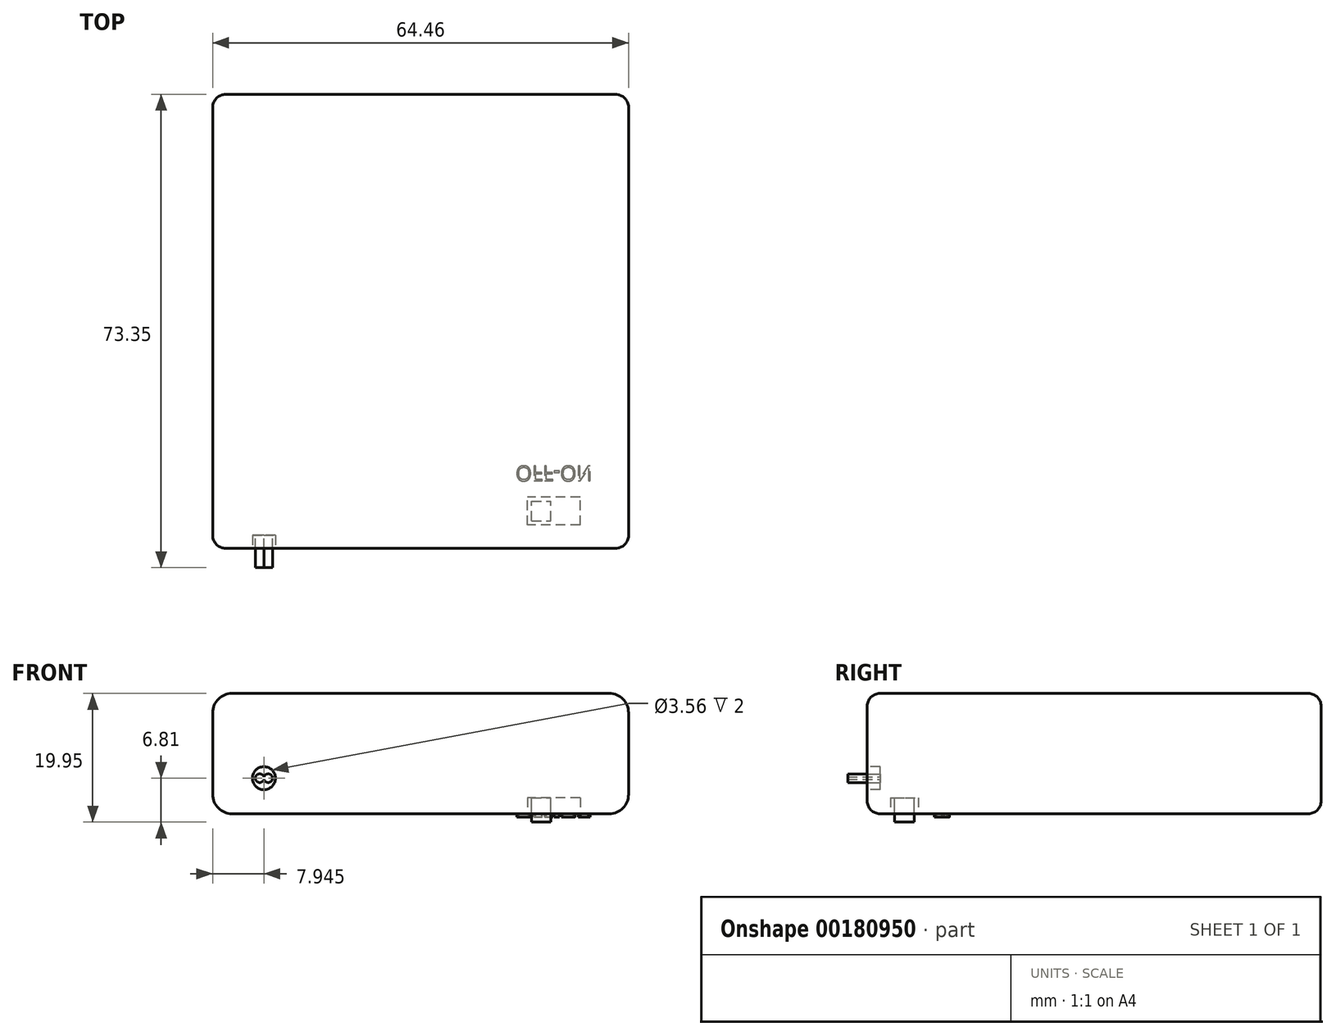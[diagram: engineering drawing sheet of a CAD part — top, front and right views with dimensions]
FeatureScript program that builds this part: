
annotation { "Feature Type Name" : "Feature", "Feature Type Description" : "" }
export const myFeature = defineFeature(function(context is Context, id is Id, definition is map)
    precondition{}
    {
        {
            var Q0;
            Q0=qCreatedBy(makeId("Top.planeOp"),FACE);
            var sketch = newSketch(context, id + "F0", { "sketchPlane" : qUnion([Q0])});
            skLineSegment(sketch, "E0.bottom", {"start": v(32.23, 35.17) * mm, "end": v(-32.23, 35.17) * mm});
            skLineSegment(sketch, "E0.top", {"start": v(32.23, -35.17) * mm, "end": v(-32.23, -35.17) * mm});
            skLineSegment(sketch, "E0.left", {"start": v(32.23, 35.17) * mm, "end": v(32.23, -35.17) * mm});
            skLineSegment(sketch, "E0.right", {"start": v(-32.23, 35.17) * mm, "end": v(-32.23, -35.17) * mm});
            skPoint(sketch, "E0.middle", {"position": v(0, 0) * mm});
            skSolve(sketch);
        }
        {
            var Q0;
            Q0=qSketchRegion(id+"F0",true);
            extrude(context, id + "F1", {"entities" : qUnion([Q0]), "depth" : 18.65 * mm});
        }
        {
            var Q0;
            Q0=makeQuery(id+"F1.opExtrude","CAP_EDGE",EDGE,{"disambiguationData":[OSD([sQuery(id+"F0.wireOp",EDGE,"E0.right")])],"isStart":false});
            var Q1;
            Q1=makeQuery(id+"F1.opExtrude","CAP_EDGE",EDGE,{"disambiguationData":[OSD([sQuery(id+"F0.wireOp",EDGE,"E0.left")])],"isStart":false});
            var Q2;
            Q2=makeQuery(id+"F1.opExtrude","CAP_EDGE",EDGE,{"disambiguationData":[OSD([sQuery(id+"F0.wireOp",EDGE,"E0.left")])],"isStart":true});
            var Q3;
            Q3=makeQuery(id+"F1.opExtrude","CAP_EDGE",EDGE,{"disambiguationData":[OSD([sQuery(id+"F0.wireOp",EDGE,"E0.right")])],"isStart":true});
            fillet(context, id + "F2", {"entities" : qUnion([Q0, Q1, Q2, Q3]), "radius" : 3 * mm, "tangentPropagation" : true, "allowEdgeOverflow" : false});
        }
        {
            var Q0;
            Q0=makeQuery(id+"F1.opExtrude","SWEPT_FACE",FACE,{"disambiguationData":[OSD([sQuery(id+"F0.wireOp",EDGE,"E0.top")])]});
            var Q1;
            Q1=makeQuery(id+"F1.opExtrude","SWEPT_FACE",FACE,{"disambiguationData":[OSD([sQuery(id+"F0.wireOp",EDGE,"E0.bottom")])]});
            fillet(context, id + "F3", {"entities" : qUnion([Q0, Q1]), "radius" : 2 * mm, "tangentPropagation" : true, "allowEdgeOverflow" : false});
        }
        {
            var Q0;
            Q0=makeQuery(id+"F1.opExtrude","CAP_FACE",FACE,{"disambiguationData":[OSD([sQuery(id+"F0.wireOp",EDGE,"E0.bottom"),sQuery(id+"F0.wireOp",EDGE,"E0.top"),sQuery(id+"F0.wireOp",EDGE,"E0.left"),sQuery(id+"F0.wireOp",EDGE,"E0.right")])],"isStart":false});
            var sketch = newSketch(context, id + "F4", { "sketchPlane" : qUnion([Q0])});
            skLineSegment(sketch, "E1.bottom", {"start": v(24.73, 31.57) * mm, "end": v(16.53, 31.57) * mm});
            skLineSegment(sketch, "E1.top", {"start": v(24.73, 27.22) * mm, "end": v(16.53, 27.22) * mm});
            skLineSegment(sketch, "E1.left", {"start": v(24.73, 31.57) * mm, "end": v(24.73, 27.22) * mm});
            skLineSegment(sketch, "E1.right", {"start": v(16.53, 31.57) * mm, "end": v(16.53, 27.22) * mm});
            skSolve(sketch);
        }
        {
            var Q0;
            Q0=qSketchRegion(id+"F4",true);
            extrude(context, id + "F5", {"entities" : qUnion([Q0]), "operationType" : NewBodyOperationType.REMOVE, "oppositeDirection" : true, "depth" : 2.5 * mm});
        }
        {
            var Q0;
            Q0=makeQuery(id+"F5.boolean.opBoolean","COPY",FACE,{"derivedFrom":makeQuery(id+"F5.opExtrude","CAP_FACE",FACE,{"disambiguationData":[OSD([sQuery(id+"F4.wireOp",EDGE,"E1.bottom"),sQuery(id+"F4.wireOp",EDGE,"E1.top"),sQuery(id+"F4.wireOp",EDGE,"E1.left"),sQuery(id+"F4.wireOp",EDGE,"E1.right")])],"isStart":false})});
            var sketch = newSketch(context, id + "F6", { "sketchPlane" : qUnion([Q0])});
            skLineSegment(sketch, "E2", {"start": v(16.53, 29.4) * mm, "end": v(24.73, 29.4) * mm, "construction": true});
            skLineSegment(sketch, "E3.bottom", {"start": v(17.2, 30.9) * mm, "end": v(20.2, 30.9) * mm});
            skLineSegment(sketch, "E3.top", {"start": v(17.2, 27.9) * mm, "end": v(20.2, 27.9) * mm});
            skLineSegment(sketch, "E3.left", {"start": v(17.2, 30.9) * mm, "end": v(17.2, 27.9) * mm});
            skLineSegment(sketch, "E3.right", {"start": v(20.2, 30.9) * mm, "end": v(20.2, 27.9) * mm});
            skPoint(sketch, "E3.middle", {"position": v(18.7, 29.4) * mm});
            skSolve(sketch);
        }
        {
            var Q0;
            Q0=qSketchRegion(id+"F6",true);
            extrude(context, id + "F7", {"entities" : qUnion([Q0]), "operationType" : NewBodyOperationType.ADD, "depth" : (1.3 + 2.5) * mm});
        }
        {
            var Q0;
            Q0=makeQuery(id+"F1.opExtrude","SWEPT_FACE",FACE,{"disambiguationData":[OSD([sQuery(id+"F0.wireOp",EDGE,"E0.bottom")])]});
            var sketch = newSketch(context, id + "F8", { "sketchPlane" : qUnion([Q0])});
            skCircle(sketch, "E4", {"center": v(24.29, 13.14) * mm, "radius": 1.78 * mm});
            skSolve(sketch);
        }
        {
            var Q0;
            Q0=qSketchRegion(id+"F8",true);
            extrude(context, id + "F9", {"entities" : qUnion([Q0]), "operationType" : NewBodyOperationType.REMOVE, "oppositeDirection" : true, "depth" : 2 * mm});
        }
        {
            var Q0;
            Q0=makeQuery(id+"F1.opExtrude","CAP_FACE",FACE,{"disambiguationData":[OSD([sQuery(id+"F0.wireOp",EDGE,"E0.bottom"),sQuery(id+"F0.wireOp",EDGE,"E0.top"),sQuery(id+"F0.wireOp",EDGE,"E0.left"),sQuery(id+"F0.wireOp",EDGE,"E0.right")])],"isStart":false});
            var sketch = newSketch(context, id + "F10", { "sketchPlane" : qUnion([Q0])});
            skText(sketch, "E5", { "text": "OFF-ON", "fontName": "OpenSans-Regular.ttf"});
            skPoint(sketch, "E6", {"position": v(20.63, 27.22) * mm});
            const initialGuessF10  = {"E5": [0.01472, 0.02242, 1, 0, 0.00233]};
            skSetInitialGuess(sketch, initialGuessF10);
            skSolve(sketch);
        }
        {
            var Q0;
            Q0=qSketchRegion(id+"F10",true);
            extrude(context, id + "F11", {"entities" : qUnion([Q0]), "operationType" : NewBodyOperationType.ADD, "depth" : 0.5 * mm});
        }
        {
            var Q0;
            Q0=makeQuery(id+"F1.opExtrude","CAP_FACE",FACE,{"disambiguationData":[OSD([sQuery(id+"F0.wireOp",EDGE,"E0.bottom"),sQuery(id+"F0.wireOp",EDGE,"E0.top"),sQuery(id+"F0.wireOp",EDGE,"E0.left"),sQuery(id+"F0.wireOp",EDGE,"E0.right")])],"isStart":true});
            var sketch = newSketch(context, id + "F12", { "sketchPlane" : qUnion([Q0])});
            skCircle(sketch, "E7", {"center": v(0, 29.19) * mm, "radius": 2.33 * mm});
            skSolve(sketch);
        }
        {
            var Q0;
            Q0=qCreatedBy(makeId("Top.planeOp"),FACE);
            var sketch = newSketch(context, id + "F13", { "sketchPlane" : qUnion([Q0])});
            skLineSegment(sketch, "E8", {"start": v(0, 61.28) * mm, "end": v(0, -59.76) * mm, "construction": true});
            skSolve(sketch);
        }
        {
            var Q0;
            Q0=makeQuery(id+"F1.opExtrude","SWEPT_BODY",BODY,{"disambiguationData":[OSD([sQuery(id+"F0.wireOp",EDGE,"E0.bottom"),sQuery(id+"F0.wireOp",EDGE,"E0.top"),sQuery(id+"F0.wireOp",EDGE,"E0.left"),sQuery(id+"F0.wireOp",EDGE,"E0.right")])]});
            var Q1;
            Q1=sQuery(id+"F13.wireOp",EDGE,"E8");
            transform(context, id + "F14", {"entities" : qUnion([Q0]), "transformType" : TransformType.ROTATION, "transformAxis" : qUnion([Q1]), "angle" : 180 * degree, "makeCopy" : false});
        }
        {
            var Q0;
            Q0=qCreatedBy(makeId("Right.planeOp"),FACE);
            var sketch = newSketch(context, id + "F15", { "sketchPlane" : qUnion([Q0])});
            skLineSegment(sketch, "E9", {"start": v(0, 0) * mm, "end": v(0, 39) * mm, "construction": true});
            skSolve(sketch);
        }
        {
            var Q0;
            Q0=makeQuery(id+"F1.opExtrude","SWEPT_BODY",BODY,{"disambiguationData":[OSD([sQuery(id+"F0.wireOp",EDGE,"E0.bottom"),sQuery(id+"F0.wireOp",EDGE,"E0.top"),sQuery(id+"F0.wireOp",EDGE,"E0.left"),sQuery(id+"F0.wireOp",EDGE,"E0.right")])]});
            var Q1;
            Q1=sQuery(id+"F15.wireOp",EDGE,"E9");
            transform(context, id + "F16", {"entities" : qUnion([Q0]), "transformType" : TransformType.ROTATION, "transformAxis" : qUnion([Q1]), "angle" : 90 * degree, "makeCopy" : false});
        }
        {
            var Q0;
            Q0=qCreatedBy(makeId("Front.planeOp"),FACE);
            var sketch = newSketch(context, id + "F17", { "sketchPlane" : qUnion([Q0])});
            skLineSegment(sketch, "E10", {"start": v(0, 0) * mm, "end": v(0, 59.82) * mm, "construction": true});
            skSolve(sketch);
        }
        {
            var Q0;
            Q0=makeQuery(id+"F1.opExtrude","SWEPT_BODY",BODY,{"disambiguationData":[OSD([sQuery(id+"F0.wireOp",EDGE,"E0.bottom"),sQuery(id+"F0.wireOp",EDGE,"E0.top"),sQuery(id+"F0.wireOp",EDGE,"E0.left"),sQuery(id+"F0.wireOp",EDGE,"E0.right")])]});
            var Q1;
            Q1=sQuery(id+"F17.wireOp",EDGE,"E10");
            transform(context, id + "F18", {"entities" : qUnion([Q0]), "transformType" : TransformType.ROTATION, "transformAxis" : qUnion([Q1]), "angle" : 90 * degree, "makeCopy" : false});
        }
        {
            var Q0;
            Q0=makeQuery(id+"F9.boolean.opBoolean","COPY",FACE,{"derivedFrom":makeQuery(id+"F9.opExtrude","CAP_FACE",FACE,{"disambiguationData":[OSD([sQuery(id+"F8.wireOp",EDGE,"E4")])],"isStart":false})});
            var sketch = newSketch(context, id + "F19", { "sketchPlane" : qUnion([Q0])});
            skLineSegment(sketch, "E11", {"start": v(-24.29, -13.14) * mm, "end": v(-24.29, -11.36) * mm, "construction": true});
            skLineSegment(sketch, "E12", {"start": v(-24.29, -11.36) * mm, "end": v(-24.29, -13.14) * mm, "construction": true});
            skArc(sketch, "E13", {"start": v(-24.29, -12.96) * mm, "mid": v(-25.6, -13.14) * mm, "end": v(-24.29, -13.32) * mm});
            skArc(sketch, "E14.MirrorC", {"start": v(-24.29, -12.96) * mm, "mid": v(-22.96, -13.14) * mm, "end": v(-24.29, -13.32) * mm});
            skSolve(sketch);
        }
        {
            var Q0;
            Q0 = qSketchRegion(id + "F19", true);
            extrude(context, id + "F20", {"entities" : qUnion([Q0]), "operationType" : NewBodyOperationType.ADD, "depth" : 5 * mm});
        }
    });
